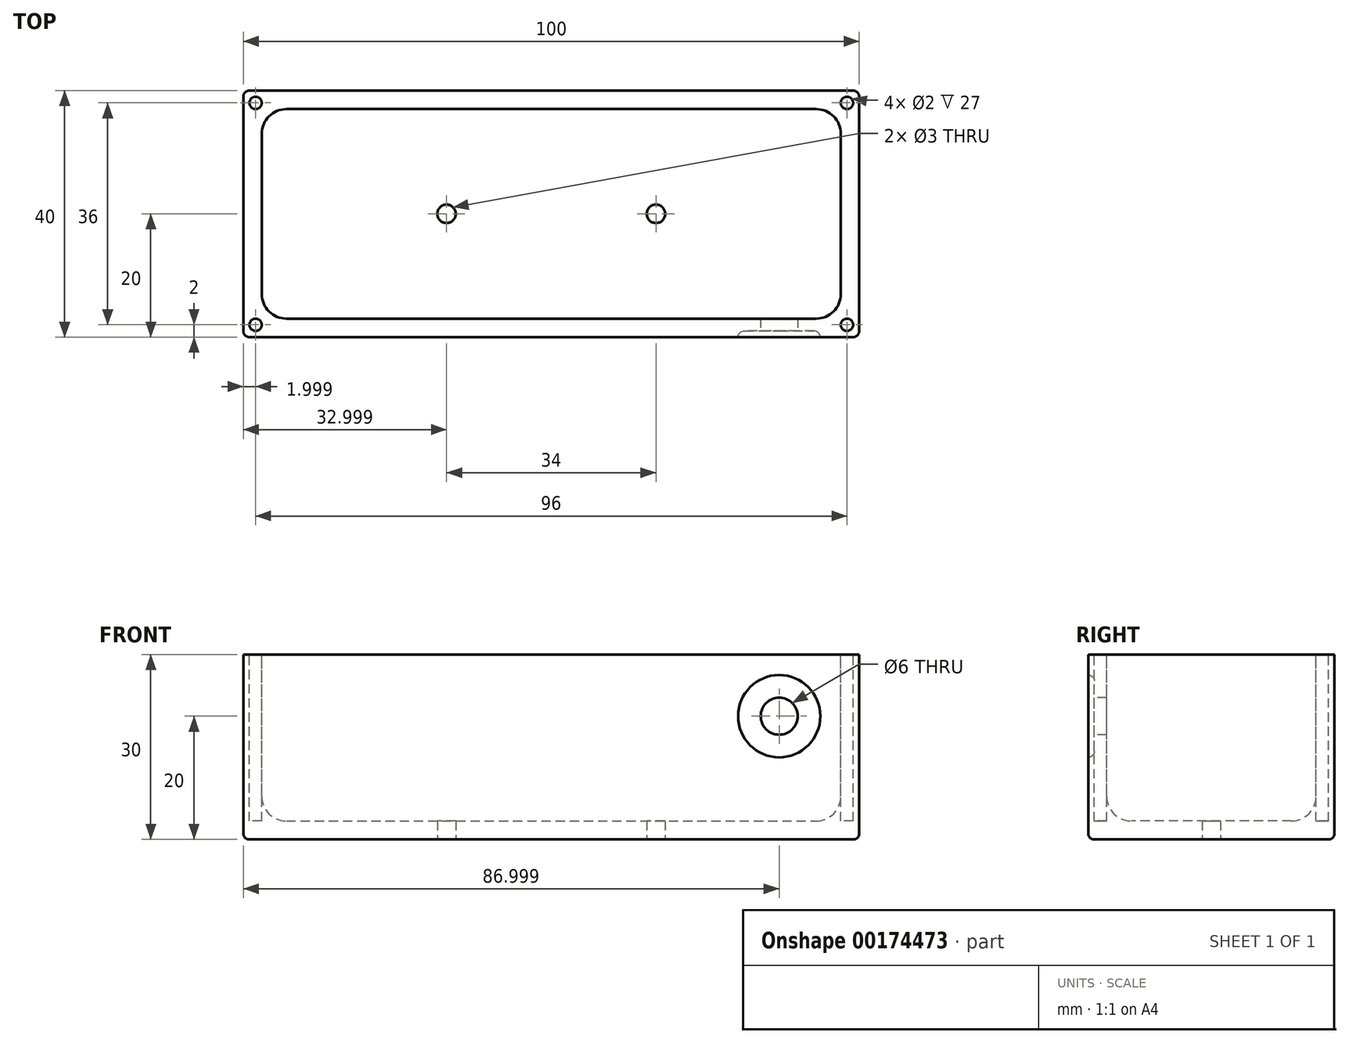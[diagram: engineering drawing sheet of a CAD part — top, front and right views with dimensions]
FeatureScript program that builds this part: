
annotation { "Feature Type Name" : "Feature", "Feature Type Description" : "" }
export const myFeature = defineFeature(function(context is Context, id is Id, definition is map)
    precondition{}
    {
        {
            var Q0;
            Q0=qCreatedBy(makeId("Top.planeOp"),FACE);
            var sketch = newSketch(context, id + "F0", { "sketchPlane" : qUnion([Q0])});
            skLineSegment(sketch, "E0.bottom", {"start": v(-54.78, 20) * mm, "end": v(45.22, 20) * mm});
            skLineSegment(sketch, "E0.top", {"start": v(-54.78, -20) * mm, "end": v(45.22, -20) * mm});
            skLineSegment(sketch, "E0.left", {"start": v(-54.78, 20) * mm, "end": v(-54.78, -20) * mm});
            skLineSegment(sketch, "E0.right", {"start": v(45.22, 20) * mm, "end": v(45.22, -20) * mm});
            skCircle(sketch, "E1", {"center": v(12.22, 0) * mm, "radius": 1.5 * mm});
            skCircle(sketch, "E2", {"center": v(-21.78, 0) * mm, "radius": 1.5 * mm});
            skSolve(sketch);
        }
        {
            var Q0;
            Q0=makeQuery(id+"F0.imprint","IMPRINT",FACE,{"disambiguationData":[TD([[makeQuery(id+"F0.imprint","IMPRINT",EDGE,{"derivedFrom":sQuery(id+"F0.wireOp",EDGE,"E0.bottom")}),-1.0]])]});
            extrude(context, id + "F1", {"entities" : qUnion([Q0]), "depth" : 30 * mm});
        }
        {
            var Q0;
            Q0=makeQuery(id+"F1.opExtrude","CAP_FACE",FACE,{"disambiguationData":[OSD([sQuery(id+"F0.wireOp",EDGE,"E0.bottom"),sQuery(id+"F0.wireOp",EDGE,"E0.top"),sQuery(id+"F0.wireOp",EDGE,"E0.left"),sQuery(id+"F0.wireOp",EDGE,"E0.right")])],"isStart":false});
            var sketch = newSketch(context, id + "F2", { "sketchPlane" : qUnion([Q0])});
            skLineSegment(sketch, "E3.bottom", {"start": v(-51.78, 17) * mm, "end": v(42.22, 17) * mm});
            skLineSegment(sketch, "E3.top", {"start": v(-51.78, -17) * mm, "end": v(42.22, -17) * mm});
            skLineSegment(sketch, "E3.left", {"start": v(-51.78, 17) * mm, "end": v(-51.78, -17) * mm});
            skLineSegment(sketch, "E3.right", {"start": v(42.22, 17) * mm, "end": v(42.22, -17) * mm});
            skCircle(sketch, "E4", {"center": v(-52.78, 18) * mm, "radius": 1 * mm});
            skCircle(sketch, "E5", {"center": v(-52.78, -18) * mm, "radius": 1 * mm});
            skCircle(sketch, "E6", {"center": v(43.22, 18) * mm, "radius": 1 * mm});
            skCircle(sketch, "E7", {"center": v(43.22, -18) * mm, "radius": 1 * mm});
            skSolve(sketch);
        }
        {
            var Q0;
            Q0 = qSketchRegion(id + "F2", true);
            extrude(context, id + "F3", {"entities" : qUnion([Q0]), "operationType" : NewBodyOperationType.REMOVE, "oppositeDirection" : true, "depth" : 27 * mm});
        }
        {
            var Q0;
            Q0=makeQuery(id+"F1.opExtrude","SWEPT_FACE",FACE,{"disambiguationData":[OSD([sQuery(id+"F0.wireOp",EDGE,"E0.top")])]});
            var sketch = newSketch(context, id + "F4", { "sketchPlane" : qUnion([Q0])});
            skCircle(sketch, "E8", {"center": v(32.22, 20) * mm, "radius": 3 * mm});
            skSolve(sketch);
        }
        {
            var Q0;
            Q0=makeQuery(id+"F4.imprint","IMPRINT",FACE,{"disambiguationData":[TD([[makeQuery(id+"F4.imprint","IMPRINT",EDGE,{"derivedFrom":sQuery(id+"F4.wireOp",EDGE,"E8")}),1.0]])]});
            extrude(context, id + "F5", {"entities" : qUnion([Q0]), "operationType" : NewBodyOperationType.REMOVE, "oppositeDirection" : true, "depth" : 5 * mm});
        }
        {
            var Q0;
            Q0=makeQuery(id+"F1.opExtrude","SWEPT_EDGE",EDGE,{"disambiguationData":[OSD([sQuery(id+"F0.wireOp",EDGE,"E0.bottom"),sQuery(id+"F0.wireOp",EDGE,"E0.right")])]});
            var Q1;
            Q1=makeQuery(id+"F1.opExtrude","CAP_EDGE",EDGE,{"disambiguationData":[OSD([sQuery(id+"F0.wireOp",EDGE,"E0.bottom")])],"isStart":true});
            var Q2;
            Q2=makeQuery(id+"F1.opExtrude","CAP_EDGE",EDGE,{"disambiguationData":[OSD([sQuery(id+"F0.wireOp",EDGE,"E0.right")])],"isStart":true});
            var Q3;
            Q3=makeQuery(id+"F1.opExtrude","SWEPT_EDGE",EDGE,{"disambiguationData":[OSD([sQuery(id+"F0.wireOp",EDGE,"E0.top"),sQuery(id+"F0.wireOp",EDGE,"E0.right")])]});
            var Q4;
            Q4=makeQuery(id+"F1.opExtrude","CAP_EDGE",EDGE,{"disambiguationData":[OSD([sQuery(id+"F0.wireOp",EDGE,"E0.top")])],"isStart":true});
            var Q5;
            Q5=makeQuery(id+"F1.opExtrude","CAP_EDGE",EDGE,{"disambiguationData":[OSD([sQuery(id+"F0.wireOp",EDGE,"E0.left")])],"isStart":true});
            var Q6;
            Q6=makeQuery(id+"F1.opExtrude","SWEPT_EDGE",EDGE,{"disambiguationData":[OSD([sQuery(id+"F0.wireOp",EDGE,"E0.bottom"),sQuery(id+"F0.wireOp",EDGE,"E0.left")])]});
            var Q7;
            Q7=makeQuery(id+"F1.opExtrude","SWEPT_EDGE",EDGE,{"disambiguationData":[OSD([sQuery(id+"F0.wireOp",EDGE,"E0.top"),sQuery(id+"F0.wireOp",EDGE,"E0.left")])]});
            fillet(context, id + "F6", {"entities" : qUnion([Q0, Q1, Q2, Q3, Q4, Q5, Q6, Q7]), "radius" : 1 * mm, "tangentPropagation" : true, "allowEdgeOverflow" : false});
        }
        {
            var Q0;
            Q0=makeQuery(id+"F3.boolean.opBoolean","COPY",EDGE,{"derivedFrom":makeQuery(id+"F3.opExtrude","SWEPT_EDGE",EDGE,{"disambiguationData":[OSD([sQuery(id+"F2.wireOp",EDGE,"E3.bottom"),sQuery(id+"F2.wireOp",EDGE,"E3.right")])]})});
            var Q1;
            Q1=makeQuery(id+"F3.boolean.opBoolean","COPY",EDGE,{"derivedFrom":makeQuery(id+"F3.opExtrude","SWEPT_EDGE",EDGE,{"disambiguationData":[OSD([sQuery(id+"F2.wireOp",EDGE,"E3.bottom"),sQuery(id+"F2.wireOp",EDGE,"E3.left")])]})});
            var Q2;
            Q2=makeQuery(id+"F3.boolean.opBoolean","COPY",EDGE,{"derivedFrom":makeQuery(id+"F3.opExtrude","SWEPT_EDGE",EDGE,{"disambiguationData":[OSD([sQuery(id+"F2.wireOp",EDGE,"E3.top"),sQuery(id+"F2.wireOp",EDGE,"E3.left")])]})});
            var Q3;
            Q3=makeQuery(id+"F3.boolean.opBoolean","COPY",EDGE,{"derivedFrom":makeQuery(id+"F3.opExtrude","SWEPT_EDGE",EDGE,{"disambiguationData":[OSD([sQuery(id+"F2.wireOp",EDGE,"E3.top"),sQuery(id+"F2.wireOp",EDGE,"E3.right")])]})});
            fillet(context, id + "F7", {"entities" : qUnion([Q0, Q1, Q2, Q3]), "radius" : 4 * mm, "tangentPropagation" : true, "allowEdgeOverflow" : false});
        }
        {
            var Q0;
            Q0=makeQuery(id+"F3.boolean.opBoolean","COPY",EDGE,{"derivedFrom":makeQuery(id+"F3.opExtrude","CAP_EDGE",EDGE,{"disambiguationData":[OSD([sQuery(id+"F2.wireOp",EDGE,"E3.bottom")])],"isStart":false})});
            fillet(context, id + "F8", {"entities" : qUnion([Q0]), "radius" : 4 * mm, "tangentPropagation" : true, "allowEdgeOverflow" : false});
        }
        {
            var Q0;
            Q0=makeQuery(id+"F1.opExtrude","SWEPT_FACE",FACE,{"disambiguationData":[OSD([sQuery(id+"F0.wireOp",EDGE,"E0.top")])]});
            var sketch = newSketch(context, id + "F9", { "sketchPlane" : qUnion([Q0])});
            skCircle(sketch, "E9", {"center": v(32.22, 20) * mm, "radius": 6.67 * mm});
            skSolve(sketch);
        }
        {
            var Q0;
            Q0 = qSketchRegion(id + "F9", true);
            extrude(context, id + "F10", {"entities" : qUnion([Q0]), "operationType" : NewBodyOperationType.REMOVE, "oppositeDirection" : true, "depth" : 1 * mm});
        }
        {
            var Q0;
            Q0=makeQuery(id+"F10.boolean.opBoolean","COPY",EDGE,{"derivedFrom":makeQuery(id+"F10.opExtrude","CAP_EDGE",EDGE,{"disambiguationData":[OSD([sQuery(id+"F9.wireOp",EDGE,"E9")])],"isStart":false})});
            fillet(context, id + "F11", {"entities" : qUnion([Q0]), "radius" : 1 * mm, "tangentPropagation" : true, "allowEdgeOverflow" : false});
        }
    });
